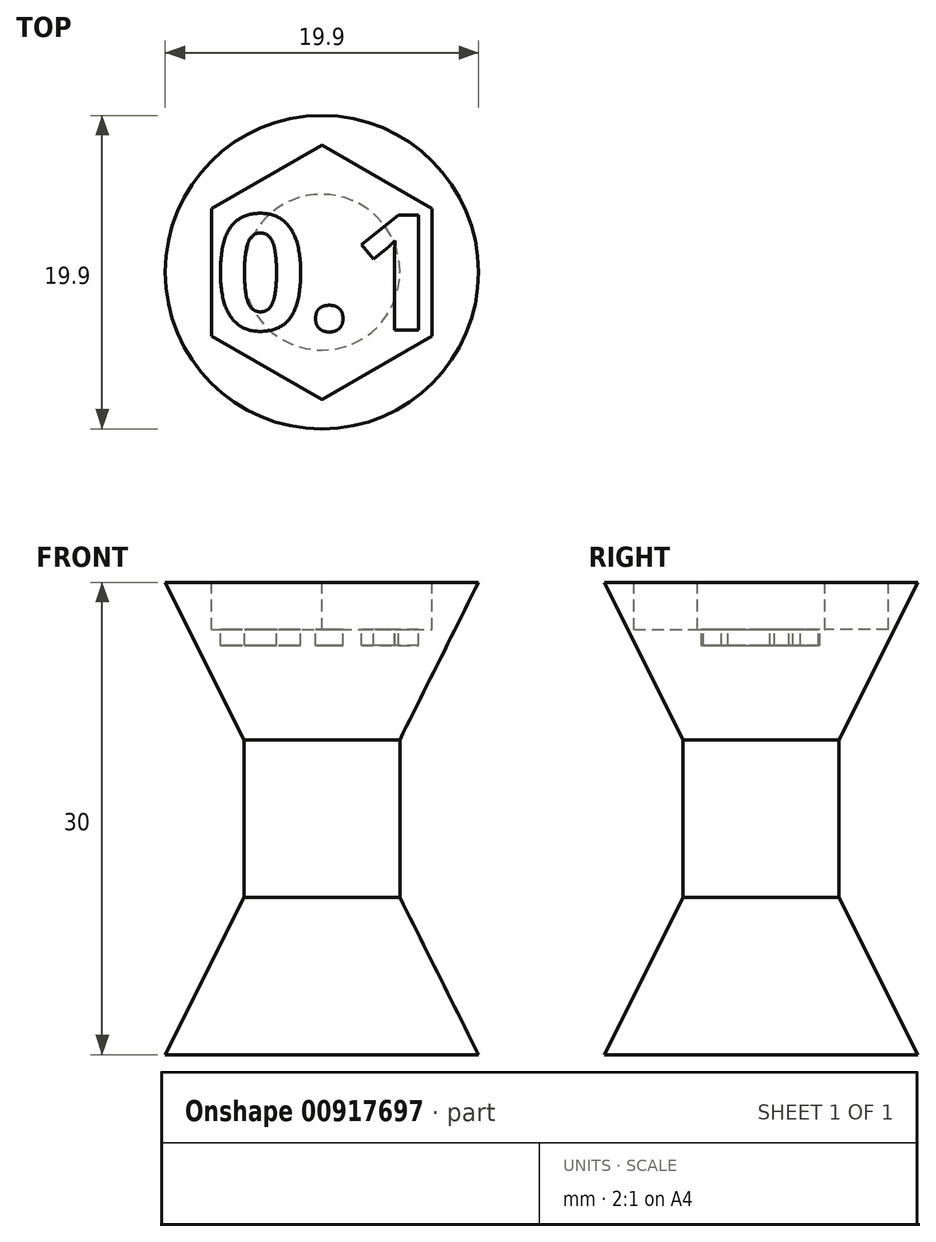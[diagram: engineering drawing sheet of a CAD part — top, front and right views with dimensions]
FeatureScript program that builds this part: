
annotation { "Feature Type Name" : "Feature", "Feature Type Description" : "" }
export const myFeature = defineFeature(function(context is Context, id is Id, definition is map)
    precondition{}
    {
        {
            var Q0;
            Q0=qCreatedBy(makeId("Front.planeOp"),FACE);
            var sketch = newSketch(context, id + "F0", { "sketchPlane" : qUnion([Q0])});
            skLineSegment(sketch, "E0", {"start": v(0, 15.03) * mm, "end": v(0, -14.97) * mm});
            skLineSegment(sketch, "E1", {"start": v(0, -14.97) * mm, "end": v(9.95, -14.97) * mm});
            skLineSegment(sketch, "E2", {"start": v(9.95, -14.97) * mm, "end": v(4.95, -4.97) * mm});
            skLineSegment(sketch, "E3", {"start": v(4.95, -4.97) * mm, "end": v(4.95, 5.03) * mm});
            skLineSegment(sketch, "E4", {"start": v(4.95, 5.03) * mm, "end": v(9.95, 15.03) * mm});
            skLineSegment(sketch, "E5", {"start": v(9.95, 15.03) * mm, "end": v(0, 15.03) * mm});
            skSolve(sketch);
        }
        {
            var Q0;
            Q0=makeQuery(id+"F0.imprint","IMPRINT",FACE,{"disambiguationData":[TD([[makeQuery(id+"F0.imprint","IMPRINT",EDGE,{"derivedFrom":sQuery(id+"F0.wireOp",EDGE,"E0")}),1.0]])]});
            var Q1;
            Q1=sQuery(id+"F0.wireOp",EDGE,"E0");
            revolve(context, id + "F1", {"surfaceOperationType" : NewSurfaceOperationType.NEW, "entities" : qUnion([Q0]), "axis" : qUnion([Q1]), "revolveType" : RevolveType.FULL});
        }
        {
            var Q0;
            Q0=makeQuery(id+"F1.opRevolve","SWEPT_FACE",FACE,{"disambiguationData":[OSD([sQuery(id+"F0.wireOp",EDGE,"E5")])]});
            var sketch = newSketch(context, id + "F2", { "sketchPlane" : qUnion([Q0])});
            skCircle(sketch, "E6.cCircle", {"center": v(0, 0) * mm, "radius": 7 * mm, "construction": true});
            skLineSegment(sketch, "E6.0", {"start": v(0, 8.08) * mm, "end": v(7, 4.04) * mm});
            skLineSegment(sketch, "E6.1", {"start": v(7, 4.04) * mm, "end": v(7, -4.04) * mm});
            skLineSegment(sketch, "E6.2", {"start": v(7, -4.04) * mm, "end": v(0, -8.08) * mm});
            skLineSegment(sketch, "E6.3", {"start": v(0, -8.08) * mm, "end": v(-7, -4.04) * mm});
            skLineSegment(sketch, "E6.4", {"start": v(-7, -4.04) * mm, "end": v(-7, 4.04) * mm});
            skLineSegment(sketch, "E6.5", {"start": v(-7, 4.04) * mm, "end": v(0, 8.08) * mm});
            skPoint(sketch, "E6.0.midPoint", {"position": v(3.5, 6.06) * mm});
            skSolve(sketch);
        }
        {
            var Q0;
            Q0 = qSketchRegion(id + "F2", true);
            extrude(context, id + "F3", {"entities" : qUnion([Q0]), "operationType" : NewBodyOperationType.REMOVE, "oppositeDirection" : true, "depth" : 3 * mm, "offsetDistance" : 25 * mm});
        }
        {
            var Q0;
            Q0=makeQuery(id+"F3.boolean.opBoolean","COPY",FACE,{"derivedFrom":makeQuery(id+"F3.opExtrude","CAP_FACE",FACE,{"disambiguationData":[OSD([sQuery(id+"F2.wireOp",EDGE,"E6.0"),sQuery(id+"F2.wireOp",EDGE,"E6.1"),sQuery(id+"F2.wireOp",EDGE,"E6.2"),sQuery(id+"F2.wireOp",EDGE,"E6.3"),sQuery(id+"F2.wireOp",EDGE,"E6.4"),sQuery(id+"F2.wireOp",EDGE,"E6.5")])],"isStart":false})});
            var sketch = newSketch(context, id + "F4", { "sketchPlane" : qUnion([Q0])});
            skText(sketch, "E7", { "text": "0.1", "fontName": "OpenSans-Bold.ttf"});
            const initialGuessF4  = {"E7": [-0.00681, -0.00366, 1, 0, 0.00735]};
            skSetInitialGuess(sketch, initialGuessF4);
            skSolve(sketch);
        }
        {
            var Q0;
            Q0=makeQuery(id+"F4.imprint","IMPRINT",FACE,{"disambiguationData":[TD([[makeQuery(id+"F4.imprint","IMPRINT",EDGE,{"derivedFrom":sQuery(id+"F4.wireOp",EDGE,"E7.sketch_text.stroke-24")}),-1.0]])]});
            var Q1;
            Q1=makeQuery(id+"F4.imprint","IMPRINT",FACE,{"disambiguationData":[TD([[makeQuery(id+"F4.imprint","IMPRINT",EDGE,{"derivedFrom":sQuery(id+"F4.wireOp",EDGE,"E7.sketch_text.stroke-16")}),-1.0]])]});
            var Q2;
            Q2=makeQuery(id+"F4.imprint","IMPRINT",FACE,{"disambiguationData":[TD([[makeQuery(id+"F4.imprint","IMPRINT",EDGE,{"derivedFrom":sQuery(id+"F4.wireOp",EDGE,"E7.sketch_text.stroke-0")}),-1.0]])]});
            extrude(context, id + "F5", {"entities" : qUnion([Q0, Q1, Q2]), "operationType" : NewBodyOperationType.REMOVE, "oppositeDirection" : true, "depth" : 1 * mm, "offsetDistance" : 25 * mm});
        }
    });
